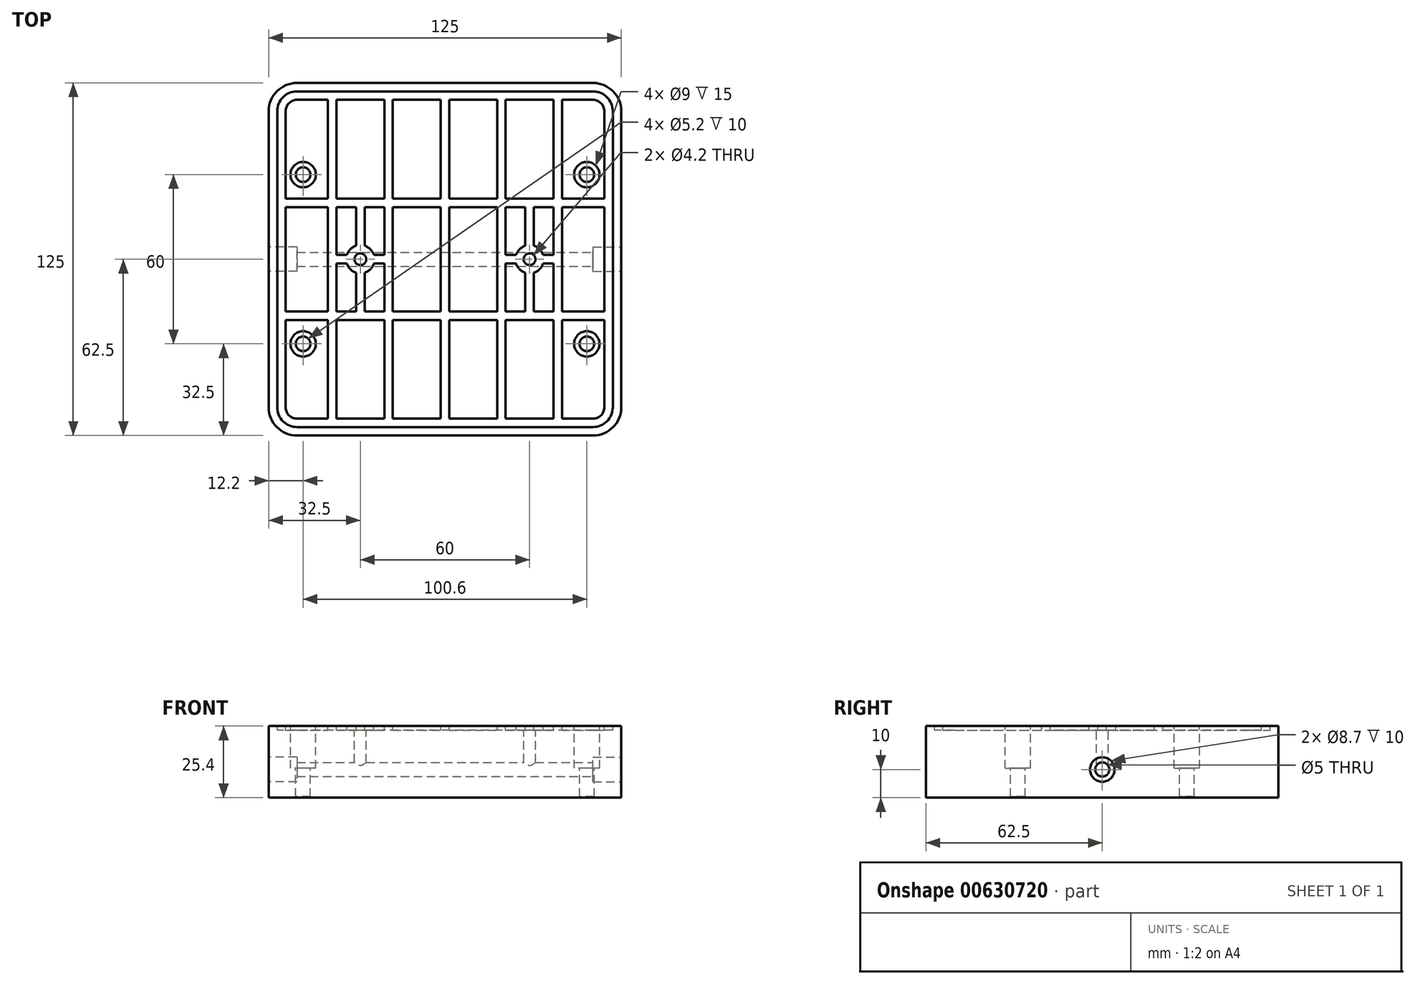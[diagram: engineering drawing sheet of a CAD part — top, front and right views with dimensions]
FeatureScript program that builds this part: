
annotation { "Feature Type Name" : "Feature", "Feature Type Description" : "" }
export const myFeature = defineFeature(function(context is Context, id is Id, definition is map)
    precondition{}
    {
        {
            var Q0;
            Q0=qCreatedBy(makeId("Top.planeOp"),FACE);
            var sketch = newSketch(context, id + "F0", { "sketchPlane" : qUnion([Q0])});
            skLineSegment(sketch, "E0.bottom", {"start": v(57.5, -72.5) * mm, "end": v(-57.5, -72.5) * mm});
            skLineSegment(sketch, "E0.top", {"start": v(57.5, 72.5) * mm, "end": v(-57.5, 72.5) * mm});
            skLineSegment(sketch, "E0.left", {"start": v(62.5, -67.5) * mm, "end": v(62.5, 67.5) * mm});
            skLineSegment(sketch, "E0.right", {"start": v(-62.5, -67.5) * mm, "end": v(-62.5, 67.5) * mm});
            skPoint(sketch, "E0.middle", {"position": v(0, 0) * mm});
            skPoint(sketch, "E1.visualSharp", {"position": v(-62.5, 72.5) * mm});
            skArc(sketch, "E1.filletArc", {"start": v(-57.5, 72.5) * mm, "mid": v(-61.04, 71.04) * mm, "end": v(-62.5, 67.5) * mm});
            skPoint(sketch, "E2.visualSharp", {"position": v(62.5, 72.5) * mm});
            skArc(sketch, "E2.filletArc", {"start": v(62.5, 67.5) * mm, "mid": v(61.04, 71.04) * mm, "end": v(57.5, 72.5) * mm});
            skPoint(sketch, "E3.visualSharp", {"position": v(62.5, -72.5) * mm});
            skArc(sketch, "E3.filletArc", {"start": v(57.5, -72.5) * mm, "mid": v(61.04, -71.04) * mm, "end": v(62.5, -67.5) * mm});
            skPoint(sketch, "E4.visualSharp", {"position": v(-62.5, -72.5) * mm});
            skArc(sketch, "E4.filletArc", {"start": v(-62.5, -67.5) * mm, "mid": v(-61.04, -71.04) * mm, "end": v(-57.5, -72.5) * mm});
            skLineSegment(sketch, "E5", {"start": v(-62.5, 67.5) * mm, "end": v(52.45, 67.5) * mm, "construction": true});
            skLineSegment(sketch, "E6", {"start": v(-48.85, -67.5) * mm, "end": v(50.9, -67.5) * mm, "construction": true});
            skCircle(sketch, "E7", {"center": v(-30, 67.5) * mm, "radius": 2.6 * mm});
            skCircle(sketch, "E8", {"center": v(30, 67.5) * mm, "radius": 2.6 * mm});
            skCircle(sketch, "E9", {"center": v(-30, -67.5) * mm, "radius": 2.6 * mm});
            skCircle(sketch, "E10", {"center": v(30, -67.5) * mm, "radius": 2.6 * mm});
            skSolve(sketch);
        }
        {
            var Q0;
            Q0=makeQuery(id+"F0.imprint","IMPRINT",FACE,{"disambiguationData":[TD([[makeQuery(id+"F0.imprint","IMPRINT",EDGE,{"derivedFrom":sQuery(id+"F0.wireOp",EDGE,"E0.bottom")}),-1.0]])]});
            extrude(context, id + "F1", {"entities" : qUnion([Q0]), "depth" : 9 * mm, "offsetDistance" : 25 * mm});
        }
        {
            var Q0;
            Q0=makeQuery(id+"F1.opExtrude","CAP_FACE",FACE,{"disambiguationData":[OSD([sQuery(id+"F0.wireOp",EDGE,"E0.bottom"),sQuery(id+"F0.wireOp",EDGE,"E0.top"),sQuery(id+"F0.wireOp",EDGE,"E0.left"),sQuery(id+"F0.wireOp",EDGE,"E0.right"),sQuery(id+"F0.wireOp",EDGE,"E1.filletArc"),sQuery(id+"F0.wireOp",EDGE,"E2.filletArc"),sQuery(id+"F0.wireOp",EDGE,"E3.filletArc"),sQuery(id+"F0.wireOp",EDGE,"E4.filletArc"),sQuery(id+"F0.wireOp",EDGE,"E7"),sQuery(id+"F0.wireOp",EDGE,"E8"),sQuery(id+"F0.wireOp",EDGE,"E9"),sQuery(id+"F0.wireOp",EDGE,"E10")])],"isStart":false});
            var sketch = newSketch(context, id + "F2", { "sketchPlane" : qUnion([Q0])});
            skLineSegment(sketch, "E11.bottom", {"start": v(52.5, -62.5) * mm, "end": v(-52.5, -62.5) * mm});
            skLineSegment(sketch, "E11.top", {"start": v(52.5, 62.5) * mm, "end": v(-52.5, 62.5) * mm});
            skLineSegment(sketch, "E11.left", {"start": v(62.5, -52.5) * mm, "end": v(62.5, 52.5) * mm});
            skLineSegment(sketch, "E11.right", {"start": v(-62.5, -52.5) * mm, "end": v(-62.5, 52.5) * mm});
            skPoint(sketch, "E11.middle", {"position": v(0, 0) * mm});
            skPoint(sketch, "E12.visualSharp", {"position": v(-62.5, 62.5) * mm});
            skArc(sketch, "E12.filletArc", {"start": v(-52.5, 62.5) * mm, "mid": v(-59.57, 59.57) * mm, "end": v(-62.5, 52.5) * mm});
            skPoint(sketch, "E13.visualSharp", {"position": v(62.5, 62.5) * mm});
            skArc(sketch, "E13.filletArc", {"start": v(62.5, 52.5) * mm, "mid": v(59.57, 59.57) * mm, "end": v(52.5, 62.5) * mm});
            skPoint(sketch, "E14.visualSharp", {"position": v(62.5, -62.5) * mm});
            skArc(sketch, "E14.filletArc", {"start": v(52.5, -62.5) * mm, "mid": v(59.57, -59.57) * mm, "end": v(62.5, -52.5) * mm});
            skPoint(sketch, "E15.visualSharp", {"position": v(-62.5, -62.5) * mm});
            skArc(sketch, "E15.filletArc", {"start": v(-62.5, -52.5) * mm, "mid": v(-59.57, -59.57) * mm, "end": v(-52.5, -62.5) * mm});
            skSolve(sketch);
        }
        {
            var Q0;
            Q0=makeQuery(id+"F2.imprint","IMPRINT",FACE,{"disambiguationData":[TD([[makeQuery(id+"F2.imprint","IMPRINT",EDGE,{"derivedFrom":sQuery(id+"F2.wireOp",EDGE,"E11.bottom")}),-1.0]])]});
            extrude(context, id + "F3", {"entities" : qUnion([Q0]), "operationType" : NewBodyOperationType.ADD, "depth" : 16.4 * mm, "offsetDistance" : 25 * mm});
        }
        {
            var Q0;
            Q0=makeQuery(id+"F3.boolean.opBoolean","MERGE",FACE,{"derivedFrom":[makeQuery(id+"F1.opExtrude","SWEPT_FACE",FACE,{"disambiguationData":[OSD([sQuery(id+"F0.wireOp",EDGE,"E0.left")])]}),makeQuery(id+"F3.opExtrude","SWEPT_FACE",FACE,{"disambiguationData":[OSD([sQuery(id+"F2.wireOp",EDGE,"E11.left")])]})]});
            var sketch = newSketch(context, id + "F4", { "sketchPlane" : qUnion([Q0])});
            skCircle(sketch, "E16", {"center": v(0, 10) * mm, "radius": 4.35 * mm});
            skCircle(sketch, "E17", {"center": v(0, 10) * mm, "radius": 2.5 * mm});
            skSolve(sketch);
        }
        {
            var Q0;
            Q0=makeQuery(id+"F4.imprint","IMPRINT",FACE,{"disambiguationData":[TD([[makeQuery(id+"F4.imprint","IMPRINT",EDGE,{"derivedFrom":sQuery(id+"F4.wireOp",EDGE,"E17")}),1.0]])]});
            extrude(context, id + "F5", {"entities" : qUnion([Q0]), "operationType" : NewBodyOperationType.REMOVE, "endBound" : BoundingType.THROUGH_ALL, "oppositeDirection" : true, "depth" : 100 * mm, "offsetDistance" : 25 * mm});
        }
        {
            var Q0;
            Q0=makeQuery(id+"F4.imprint","IMPRINT",FACE,{"disambiguationData":[TD([[makeQuery(id+"F4.imprint","IMPRINT",EDGE,{"derivedFrom":sQuery(id+"F4.wireOp",EDGE,"E16")}),1.0]])]});
            extrude(context, id + "F6", {"entities" : qUnion([Q0]), "operationType" : NewBodyOperationType.REMOVE, "oppositeDirection" : true, "depth" : 10 * mm, "offsetDistance" : 25 * mm});
        }
        {
            var Q0;
            {var subQ0=sQuery(id+"F0.wireOp",EDGE,"E4.filletArc");var subQ1=sQuery(id+"F0.wireOp",EDGE,"E10");var subQ2=sQuery(id+"F0.wireOp",EDGE,"E0.left");var subQ3=sQuery(id+"F0.wireOp",EDGE,"E9");var subQ4=sQuery(id+"F0.wireOp",EDGE,"E0.bottom");var subQ5=sQuery(id+"F0.wireOp",EDGE,"E3.filletArc");var subQ6=sQuery(id+"F0.wireOp",EDGE,"E0.right");Q0=makeQuery(id+"F3.boolean.opBoolean","SPLIT",FACE,{"disambiguationData":[TD([makeQuery(id+"F1.opExtrude","SWEPT_FACE",FACE,{"disambiguationData":[OSD([subQ4])]})])],"derivedFrom":makeQuery(id+"F1.opExtrude","CAP_FACE",FACE,{"disambiguationData":[OSD([subQ4,sQuery(id+"F0.wireOp",EDGE,"E0.top"),subQ2,subQ6,sQuery(id+"F0.wireOp",EDGE,"E1.filletArc"),sQuery(id+"F0.wireOp",EDGE,"E2.filletArc"),subQ5,subQ0,sQuery(id+"F0.wireOp",EDGE,"E7"),sQuery(id+"F0.wireOp",EDGE,"E8"),subQ3,subQ1])],"isStart":false})});}
            var Q1;
            {var subQ0=sQuery(id+"F0.wireOp",EDGE,"E8");var subQ1=sQuery(id+"F0.wireOp",EDGE,"E7");var subQ2=sQuery(id+"F0.wireOp",EDGE,"E2.filletArc");var subQ3=sQuery(id+"F0.wireOp",EDGE,"E0.top");var subQ4=sQuery(id+"F0.wireOp",EDGE,"E0.left");var subQ5=sQuery(id+"F0.wireOp",EDGE,"E0.right");var subQ6=sQuery(id+"F0.wireOp",EDGE,"E1.filletArc");Q1=makeQuery(id+"F3.boolean.opBoolean","SPLIT",FACE,{"disambiguationData":[TD([makeQuery(id+"F1.opExtrude","SWEPT_FACE",FACE,{"disambiguationData":[OSD([subQ3])]})])],"derivedFrom":makeQuery(id+"F1.opExtrude","CAP_FACE",FACE,{"disambiguationData":[OSD([sQuery(id+"F0.wireOp",EDGE,"E0.bottom"),subQ3,subQ4,subQ5,subQ6,subQ2,sQuery(id+"F0.wireOp",EDGE,"E3.filletArc"),sQuery(id+"F0.wireOp",EDGE,"E4.filletArc"),subQ1,subQ0,sQuery(id+"F0.wireOp",EDGE,"E9"),sQuery(id+"F0.wireOp",EDGE,"E10")])],"isStart":false})});}
            extrude(context, id + "F7", {"entities" : qUnion([Q0, Q1]), "operationType" : NewBodyOperationType.REMOVE, "oppositeDirection" : true, "depth" : 25 * mm, "offsetDistance" : 25 * mm});
        }
        {
            var Q0;
            Q0=makeQuery(id+"F3.opExtrude","CAP_FACE",FACE,{"disambiguationData":[OSD([sQuery(id+"F2.wireOp",EDGE,"E11.bottom"),sQuery(id+"F2.wireOp",EDGE,"E11.top"),sQuery(id+"F2.wireOp",EDGE,"E11.left"),sQuery(id+"F2.wireOp",EDGE,"E11.right"),sQuery(id+"F2.wireOp",EDGE,"E12.filletArc"),sQuery(id+"F2.wireOp",EDGE,"E13.filletArc"),sQuery(id+"F2.wireOp",EDGE,"E14.filletArc"),sQuery(id+"F2.wireOp",EDGE,"E15.filletArc")])],"isStart":false});
            var sketch = newSketch(context, id + "F8", { "sketchPlane" : qUnion([Q0])});
            skCircle(sketch, "E18", {"center": v(-50.3, 30) * mm, "radius": 4.5 * mm});
            skCircle(sketch, "E19", {"center": v(50.3, 30) * mm, "radius": 4.5 * mm});
            skCircle(sketch, "E20", {"center": v(-50.3, -30) * mm, "radius": 4.5 * mm});
            skCircle(sketch, "E21", {"center": v(50.3, -30) * mm, "radius": 4.5 * mm});
            skLineSegment(sketch, "E22.bottom", {"start": v(24.32, -16.82) * mm, "end": v(-24.32, -16.82) * mm, "construction": true});
            skLineSegment(sketch, "E22.top", {"start": v(24.32, 16.82) * mm, "end": v(-24.32, 16.82) * mm, "construction": true});
            skLineSegment(sketch, "E22.left", {"start": v(24.32, -16.82) * mm, "end": v(24.32, 16.82) * mm, "construction": true});
            skLineSegment(sketch, "E22.right", {"start": v(-24.32, -16.82) * mm, "end": v(-24.32, 16.82) * mm, "construction": true});
            skPoint(sketch, "E22.middle", {"position": v(0, 0) * mm});
            skSolve(sketch);
        }
        {
            var Q0;
            Q0 = qSketchRegion(id + "F8", true);
            extrude(context, id + "F9", {"entities" : qUnion([Q0]), "operationType" : NewBodyOperationType.REMOVE, "oppositeDirection" : true, "depth" : 15 * mm, "offsetDistance" : 25 * mm});
        }
        {
            var Q0;
            Q0=makeQuery(id+"F3.opExtrude","CAP_FACE",FACE,{"disambiguationData":[OSD([sQuery(id+"F2.wireOp",EDGE,"E11.bottom"),sQuery(id+"F2.wireOp",EDGE,"E11.top"),sQuery(id+"F2.wireOp",EDGE,"E11.left"),sQuery(id+"F2.wireOp",EDGE,"E11.right"),sQuery(id+"F2.wireOp",EDGE,"E12.filletArc"),sQuery(id+"F2.wireOp",EDGE,"E13.filletArc"),sQuery(id+"F2.wireOp",EDGE,"E14.filletArc"),sQuery(id+"F2.wireOp",EDGE,"E15.filletArc")])],"isStart":false});
            var sketch = newSketch(context, id + "F10", { "sketchPlane" : qUnion([Q0])});
            skCircle(sketch, "E23", {"center": v(-50.3, 30) * mm, "radius": 4 * mm});
            skCircle(sketch, "E24", {"center": v(50.3, 30) * mm, "radius": 4 * mm});
            skCircle(sketch, "E25", {"center": v(50.3, -30) * mm, "radius": 4 * mm});
            skCircle(sketch, "E26", {"center": v(-50.3, -30) * mm, "radius": 4 * mm});
            skSolve(sketch);
        }
        {
            var Q0;
            Q0=makeQuery(id+"F3.opExtrude","CAP_FACE",FACE,{"disambiguationData":[OSD([sQuery(id+"F2.wireOp",EDGE,"E11.bottom"),sQuery(id+"F2.wireOp",EDGE,"E11.top"),sQuery(id+"F2.wireOp",EDGE,"E11.left"),sQuery(id+"F2.wireOp",EDGE,"E11.right"),sQuery(id+"F2.wireOp",EDGE,"E12.filletArc"),sQuery(id+"F2.wireOp",EDGE,"E13.filletArc"),sQuery(id+"F2.wireOp",EDGE,"E14.filletArc"),sQuery(id+"F2.wireOp",EDGE,"E15.filletArc")])],"isStart":false});
            var sketch = newSketch(context, id + "F11", { "sketchPlane" : qUnion([Q0])});
            skCircle(sketch, "E27", {"center": v(-50.3, 30) * mm, "radius": 2.6 * mm});
            skCircle(sketch, "E28", {"center": v(50.3, 30) * mm, "radius": 2.6 * mm});
            skCircle(sketch, "E29", {"center": v(50.3, -30) * mm, "radius": 2.6 * mm});
            skCircle(sketch, "E30", {"center": v(-50.3, -30) * mm, "radius": 2.6 * mm});
            skSolve(sketch);
        }
        {
            var Q0;
            Q0 = qSketchRegion(id + "F11", true);
            extrude(context, id + "F12", {"entities" : qUnion([Q0]), "operationType" : NewBodyOperationType.REMOVE, "oppositeDirection" : true, "depth" : 25 * mm, "offsetDistance" : 25 * mm});
        }
        {
            var Q0;
            Q0=makeQuery(id+"F3.opExtrude","CAP_FACE",FACE,{"disambiguationData":[OSD([sQuery(id+"F2.wireOp",EDGE,"E11.bottom"),sQuery(id+"F2.wireOp",EDGE,"E11.top"),sQuery(id+"F2.wireOp",EDGE,"E11.left"),sQuery(id+"F2.wireOp",EDGE,"E11.right"),sQuery(id+"F2.wireOp",EDGE,"E12.filletArc"),sQuery(id+"F2.wireOp",EDGE,"E13.filletArc"),sQuery(id+"F2.wireOp",EDGE,"E14.filletArc"),sQuery(id+"F2.wireOp",EDGE,"E15.filletArc")])],"isStart":false});
            var sketch = newSketch(context, id + "F13", { "sketchPlane" : qUnion([Q0])});
            skLineSegment(sketch, "E31.0.0", {"start": v(62.5, -52.5) * mm, "end": v(62.5, 52.5) * mm});
            skArc(sketch, "E31.0.1", {"start": v(62.5, 52.5) * mm, "mid": v(59.57, 59.57) * mm, "end": v(52.5, 62.5) * mm});
            skLineSegment(sketch, "E31.0.2", {"start": v(52.5, 62.5) * mm, "end": v(-52.5, 62.5) * mm});
            skArc(sketch, "E31.0.3", {"start": v(-52.5, 62.5) * mm, "mid": v(-59.57, 59.57) * mm, "end": v(-62.5, 52.5) * mm});
            skLineSegment(sketch, "E31.0.4", {"start": v(-62.5, 52.5) * mm, "end": v(-62.5, -52.5) * mm});
            skArc(sketch, "E31.0.5", {"start": v(-62.5, -52.5) * mm, "mid": v(-59.57, -59.57) * mm, "end": v(-52.5, -62.5) * mm});
            skLineSegment(sketch, "E31.0.6", {"start": v(-52.5, -62.5) * mm, "end": v(52.5, -62.5) * mm});
            skArc(sketch, "E31.0.7", {"start": v(52.5, -62.5) * mm, "mid": v(59.57, -59.57) * mm, "end": v(62.5, -52.5) * mm});
            skArc(sketch, "E32.0", {"start": v(59.5, 52.5) * mm, "mid": v(57.45, 57.45) * mm, "end": v(52.5, 59.5) * mm});
            skLineSegment(sketch, "E32.1", {"start": v(59.5, -52.5) * mm, "end": v(59.5, 52.5) * mm});
            skLineSegment(sketch, "E32.2", {"start": v(52.5, 59.5) * mm, "end": v(-52.5, 59.5) * mm});
            skArc(sketch, "E32.3", {"start": v(52.5, -59.5) * mm, "mid": v(57.45, -57.45) * mm, "end": v(59.5, -52.5) * mm});
            skArc(sketch, "E32.4", {"start": v(-52.5, 59.5) * mm, "mid": v(-57.45, 57.45) * mm, "end": v(-59.5, 52.5) * mm});
            skLineSegment(sketch, "E32.5", {"start": v(-59.5, 52.5) * mm, "end": v(-59.5, -52.5) * mm});
            skArc(sketch, "E32.6", {"start": v(-59.5, -52.5) * mm, "mid": v(-57.45, -57.45) * mm, "end": v(-52.5, -59.5) * mm});
            skLineSegment(sketch, "E32.7", {"start": v(-52.5, -59.5) * mm, "end": v(52.5, -59.5) * mm});
            skLineSegment(sketch, "E33.0", {"start": v(52.5, 56.5) * mm, "end": v(-52.5, 56.5) * mm});
            skArc(sketch, "E33.1", {"start": v(56.5, 52.5) * mm, "mid": v(55.33, 55.33) * mm, "end": v(52.5, 56.5) * mm});
            skArc(sketch, "E33.2", {"start": v(-52.5, 56.5) * mm, "mid": v(-55.33, 55.33) * mm, "end": v(-56.5, 52.5) * mm});
            skLineSegment(sketch, "E33.3", {"start": v(56.5, -52.5) * mm, "end": v(56.5, 52.5) * mm});
            skLineSegment(sketch, "E33.4", {"start": v(-56.5, 52.5) * mm, "end": v(-56.5, -52.5) * mm});
            skArc(sketch, "E33.5", {"start": v(-56.5, -52.5) * mm, "mid": v(-55.33, -55.33) * mm, "end": v(-52.5, -56.5) * mm});
            skLineSegment(sketch, "E33.6", {"start": v(-52.5, -56.5) * mm, "end": v(52.5, -56.5) * mm});
            skArc(sketch, "E33.7", {"start": v(52.5, -56.5) * mm, "mid": v(55.33, -55.33) * mm, "end": v(56.5, -52.5) * mm});
            skLineSegment(sketch, "E34", {"start": v(-56.5, 0) * mm, "end": v(56.5, 0) * mm, "construction": true});
            skLineSegment(sketch, "E35.0.1.0", {"start": v(-56.5, 21.5) * mm, "end": v(56.5, 21.5) * mm});
            skLineSegment(sketch, "E35.0.1.1", {"start": v(-56.5, 18.5) * mm, "end": v(56.5, 18.5) * mm});
            skLineSegment(sketch, "E35.direction1", {"start": v(-56.5, -1.5) * mm, "end": v(-31.5, -1.5) * mm, "construction": true});
            skLineSegment(sketch, "E35.direction2", {"start": v(-56.5, -1.5) * mm, "end": v(-56.5, 18.5) * mm, "construction": true});
            skLineSegment(sketch, "E36.MirrorCS", {"start": v(-56.5, -18.5) * mm, "end": v(56.5, -18.5) * mm});
            skLineSegment(sketch, "E37.MirrorCS", {"start": v(-56.5, -21.5) * mm, "end": v(56.5, -21.5) * mm});
            skSolve(sketch);
        }
        {
            var Q0;
            Q0=makeQuery(id+"F13.imprint","IMPRINT",FACE,{"disambiguationData":[TD([[makeQuery(id+"F13.imprint","IMPRINT",EDGE,{"derivedFrom":sQuery(id+"F13.wireOp",EDGE,"E32.0")}),1.0]])]});
            var Q1;
            {var subQ0=sQuery(id+"F13.wireOp",EDGE,"E35.0.2.0");Q1=makeQuery(id+"F13.imprint","IMPRINT",FACE,{"disambiguationData":[TD([[makeQuery(id+"F13.imprint","IMPRINT",EDGE,{"derivedFrom":subQ0}),-1.0]])]});}
            var Q2;
            {var subQ0=sQuery(id+"F13.wireOp",EDGE,"E35.0.1.0");Q2=makeQuery(id+"F13.imprint","IMPRINT",FACE,{"disambiguationData":[TD([[makeQuery(id+"F13.imprint","IMPRINT",EDGE,{"derivedFrom":subQ0}),-1.0]])]});}
            var Q3;
            {var subQ0=sQuery(id+"F13.wireOp",EDGE,"E36.MirrorCS");Q3=makeQuery(id+"F13.imprint","IMPRINT",FACE,{"disambiguationData":[TD([[makeQuery(id+"F13.imprint","IMPRINT",EDGE,{"derivedFrom":subQ0}),-1.0]])]});}
            var Q4;
            {var subQ0=sQuery(id+"F13.wireOp",EDGE,"df780f31-4266-4d93-95b3-dd8d206b99b12.MirrorCS");Q4=makeQuery(id+"F13.imprint","IMPRINT",FACE,{"disambiguationData":[TD([[makeQuery(id+"F13.imprint","IMPRINT",EDGE,{"derivedFrom":subQ0}),1.0]])]});}
            var Q5;
            {var subQ0=sQuery(id+"F13.wireOp",EDGE,"0d607146-ac1c-4b7b-96e5-c2cd56f04a76.0.left");Q5=makeQuery(id+"F13.imprint","IMPRINT",FACE,{"disambiguationData":[TD([[makeQuery(id+"F13.imprint","IMPRINT",EDGE,{"derivedFrom":subQ0}),-1.0]])]});}
            extrude(context, id + "F14", {"entities" : qUnion([Q0, Q1, Q2, Q3, Q4, Q5]), "operationType" : NewBodyOperationType.REMOVE, "oppositeDirection" : true, "depth" : 1.5 * mm, "offsetDistance" : 25 * mm});
        }
        {
            var Q0;
            Q0=makeQuery(id+"F14.boolean.opBoolean","SPLIT",FACE,{"disambiguationData":[TD([makeQuery(id+"F9.boolean.opBoolean","COPY",FACE,{"derivedFrom":makeQuery(id+"F9.opExtrude","SWEPT_FACE",FACE,{"disambiguationData":[OSD([sQuery(id+"F8.wireOp",EDGE,"E18")])]})})])],"derivedFrom":makeQuery(id+"F3.opExtrude","CAP_FACE",FACE,{"disambiguationData":[OSD([sQuery(id+"F2.wireOp",EDGE,"E11.bottom"),sQuery(id+"F2.wireOp",EDGE,"E11.top"),sQuery(id+"F2.wireOp",EDGE,"E11.left"),sQuery(id+"F2.wireOp",EDGE,"E11.right"),sQuery(id+"F2.wireOp",EDGE,"E12.filletArc"),sQuery(id+"F2.wireOp",EDGE,"E13.filletArc"),sQuery(id+"F2.wireOp",EDGE,"E14.filletArc"),sQuery(id+"F2.wireOp",EDGE,"E15.filletArc")])],"isStart":false})});
            var sketch = newSketch(context, id + "F15", { "sketchPlane" : qUnion([Q0])});
            skLineSegment(sketch, "E38", {"start": v(0, -56.5) * mm, "end": v(0, 56.5) * mm, "construction": true});
            skLineSegment(sketch, "E39.0.left", {"start": v(-1.5, -56.5) * mm, "end": v(-1.5, 56.5) * mm});
            skLineSegment(sketch, "E39.0.right", {"start": v(1.5, -56.5) * mm, "end": v(1.5, 56.5) * mm});
            skLineSegment(sketch, "E40.1.0.0", {"start": v(18.5, -56.5) * mm, "end": v(18.5, 56.5) * mm});
            skLineSegment(sketch, "E40.1.0.1", {"start": v(21.5, -56.5) * mm, "end": v(21.5, 56.5) * mm});
            skLineSegment(sketch, "E40.2.0.0", {"start": v(38.5, -56.5) * mm, "end": v(38.5, 56.5) * mm});
            skLineSegment(sketch, "E40.2.0.1", {"start": v(41.5, -56.5) * mm, "end": v(41.5, 56.5) * mm});
            skLineSegment(sketch, "E40.direction1", {"start": v(-1.5, -56.5) * mm, "end": v(18.5, -56.5) * mm, "construction": true});
            skLineSegment(sketch, "E41.MirrorCS", {"start": v(-41.5, -56.5) * mm, "end": v(-41.5, 56.5) * mm});
            skLineSegment(sketch, "E42.MirrorCS", {"start": v(-38.5, -56.5) * mm, "end": v(-38.5, 56.5) * mm});
            skLineSegment(sketch, "E43.MirrorCS", {"start": v(-18.5, -56.5) * mm, "end": v(-18.5, 56.5) * mm});
            skLineSegment(sketch, "E44.MirrorCS", {"start": v(-21.5, -56.5) * mm, "end": v(-21.5, 56.5) * mm});
            skLineSegment(sketch, "E45", {"start": v(-41.5, 56.5) * mm, "end": v(41.5, 56.5) * mm});
            skLineSegment(sketch, "E46", {"start": v(41.5, -56.5) * mm, "end": v(-41.5, -56.5) * mm});
            skSolve(sketch);
        }
        {
            var Q0;
            {var subQ0=sQuery(id+"F15.wireOp",EDGE,"E45");var subQ1=sQuery(id+"F15.wireOp",EDGE,"E41.MirrorCS");var subQ2=makeQuery(id+"F15.imprint","INTERSECT",VERTEX,{"derivedFrom":[subQ1,subQ0]});Q0=makeQuery(id+"F15.imprint","IMPRINT",FACE,{"disambiguationData":[TD([[makeQuery(id+"F15.imprint","IMPRINT",EDGE,{"disambiguationData":[TD([[subQ2,1.0]])],"derivedFrom":subQ1}),-1.0]])]});}
            var Q1;
            {var subQ0=sQuery(id+"F15.wireOp",EDGE,"E41.MirrorCS");var subQ1=makeQuery(id+"F14.boolean.opBoolean","COPY",EDGE,{"derivedFrom":makeQuery(id+"F14.opExtrude","CAP_EDGE",EDGE,{"disambiguationData":[OSD([sQuery(id+"F13.wireOp",EDGE,"E35.0.1.0")])],"isStart":true})});var subQ2=makeQuery(id+"F15.imprint","INTERSECT",VERTEX,{"derivedFrom":[subQ1,subQ0]});Q1=makeQuery(id+"F15.imprint","IMPRINT",FACE,{"disambiguationData":[TD([[makeQuery(id+"F15.imprint","IMPRINT",EDGE,{"disambiguationData":[TD([[subQ2,-1.0]])],"derivedFrom":subQ0}),-1.0]])]});}
            var Q2;
            {var subQ0=sQuery(id+"F15.wireOp",EDGE,"E46");var subQ1=sQuery(id+"F15.wireOp",EDGE,"E41.MirrorCS");var subQ2=makeQuery(id+"F15.imprint","INTERSECT",VERTEX,{"derivedFrom":[subQ1,subQ0]});Q2=makeQuery(id+"F15.imprint","IMPRINT",FACE,{"disambiguationData":[TD([[makeQuery(id+"F15.imprint","IMPRINT",EDGE,{"disambiguationData":[TD([[subQ2,-1.0]])],"derivedFrom":subQ1}),-1.0]])]});}
            var Q3;
            {var subQ0=sQuery(id+"F15.wireOp",EDGE,"E45");var subQ1=sQuery(id+"F15.wireOp",EDGE,"E43.MirrorCS");var subQ2=makeQuery(id+"F15.imprint","INTERSECT",VERTEX,{"derivedFrom":[subQ1,subQ0]});Q3=makeQuery(id+"F15.imprint","IMPRINT",FACE,{"disambiguationData":[TD([[makeQuery(id+"F15.imprint","IMPRINT",EDGE,{"disambiguationData":[TD([[subQ2,1.0]])],"derivedFrom":subQ1}),1.0]])]});}
            var Q4;
            {var subQ0=sQuery(id+"F15.wireOp",EDGE,"E43.MirrorCS");var subQ1=makeQuery(id+"F14.boolean.opBoolean","COPY",EDGE,{"derivedFrom":makeQuery(id+"F14.opExtrude","CAP_EDGE",EDGE,{"disambiguationData":[OSD([sQuery(id+"F13.wireOp",EDGE,"E35.0.1.0")])],"isStart":true})});var subQ2=makeQuery(id+"F15.imprint","INTERSECT",VERTEX,{"derivedFrom":[subQ1,subQ0]});Q4=makeQuery(id+"F15.imprint","IMPRINT",FACE,{"disambiguationData":[TD([[makeQuery(id+"F15.imprint","IMPRINT",EDGE,{"disambiguationData":[TD([[subQ2,-1.0]])],"derivedFrom":subQ0}),1.0]])]});}
            var Q5;
            {var subQ0=sQuery(id+"F15.wireOp",EDGE,"E46");var subQ1=sQuery(id+"F15.wireOp",EDGE,"E43.MirrorCS");var subQ2=makeQuery(id+"F15.imprint","INTERSECT",VERTEX,{"derivedFrom":[subQ1,subQ0]});Q5=makeQuery(id+"F15.imprint","IMPRINT",FACE,{"disambiguationData":[TD([[makeQuery(id+"F15.imprint","IMPRINT",EDGE,{"disambiguationData":[TD([[subQ2,-1.0]])],"derivedFrom":subQ1}),1.0]])]});}
            var Q6;
            {var subQ0=sQuery(id+"F15.wireOp",EDGE,"E45");var subQ1=sQuery(id+"F15.wireOp",EDGE,"E39.0.left");var subQ2=makeQuery(id+"F15.imprint","INTERSECT",VERTEX,{"derivedFrom":[subQ1,subQ0]});Q6=makeQuery(id+"F15.imprint","IMPRINT",FACE,{"disambiguationData":[TD([[makeQuery(id+"F15.imprint","IMPRINT",EDGE,{"disambiguationData":[TD([[subQ2,1.0]])],"derivedFrom":subQ1}),-1.0]])]});}
            var Q7;
            {var subQ0=sQuery(id+"F15.wireOp",EDGE,"E39.0.left");var subQ1=makeQuery(id+"F14.boolean.opBoolean","COPY",EDGE,{"derivedFrom":makeQuery(id+"F14.opExtrude","CAP_EDGE",EDGE,{"disambiguationData":[OSD([sQuery(id+"F13.wireOp",EDGE,"E35.0.1.0")])],"isStart":true})});var subQ2=makeQuery(id+"F15.imprint","INTERSECT",VERTEX,{"derivedFrom":[subQ1,subQ0]});Q7=makeQuery(id+"F15.imprint","IMPRINT",FACE,{"disambiguationData":[TD([[makeQuery(id+"F15.imprint","IMPRINT",EDGE,{"disambiguationData":[TD([[subQ2,-1.0]])],"derivedFrom":subQ0}),-1.0]])]});}
            var Q8;
            {var subQ0=sQuery(id+"F15.wireOp",EDGE,"E46");var subQ1=sQuery(id+"F15.wireOp",EDGE,"E39.0.left");var subQ2=makeQuery(id+"F15.imprint","INTERSECT",VERTEX,{"derivedFrom":[subQ1,subQ0]});Q8=makeQuery(id+"F15.imprint","IMPRINT",FACE,{"disambiguationData":[TD([[makeQuery(id+"F15.imprint","IMPRINT",EDGE,{"disambiguationData":[TD([[subQ2,-1.0]])],"derivedFrom":subQ1}),-1.0]])]});}
            var Q9;
            {var subQ0=sQuery(id+"F15.wireOp",EDGE,"E46");var subQ1=sQuery(id+"F15.wireOp",EDGE,"E40.1.0.0");var subQ2=makeQuery(id+"F15.imprint","INTERSECT",VERTEX,{"derivedFrom":[subQ1,subQ0]});Q9=makeQuery(id+"F15.imprint","IMPRINT",FACE,{"disambiguationData":[TD([[makeQuery(id+"F15.imprint","IMPRINT",EDGE,{"disambiguationData":[TD([[subQ2,-1.0]])],"derivedFrom":subQ1}),-1.0]])]});}
            var Q10;
            {var subQ0=sQuery(id+"F15.wireOp",EDGE,"E40.1.0.0");var subQ1=makeQuery(id+"F14.boolean.opBoolean","COPY",EDGE,{"derivedFrom":makeQuery(id+"F14.opExtrude","CAP_EDGE",EDGE,{"disambiguationData":[OSD([sQuery(id+"F13.wireOp",EDGE,"E35.0.1.0")])],"isStart":true})});var subQ2=makeQuery(id+"F15.imprint","INTERSECT",VERTEX,{"derivedFrom":[subQ1,subQ0]});Q10=makeQuery(id+"F15.imprint","IMPRINT",FACE,{"disambiguationData":[TD([[makeQuery(id+"F15.imprint","IMPRINT",EDGE,{"disambiguationData":[TD([[subQ2,-1.0]])],"derivedFrom":subQ0}),-1.0]])]});}
            var Q11;
            {var subQ0=sQuery(id+"F15.wireOp",EDGE,"E45");var subQ1=sQuery(id+"F15.wireOp",EDGE,"E40.1.0.0");var subQ2=makeQuery(id+"F15.imprint","INTERSECT",VERTEX,{"derivedFrom":[subQ1,subQ0]});Q11=makeQuery(id+"F15.imprint","IMPRINT",FACE,{"disambiguationData":[TD([[makeQuery(id+"F15.imprint","IMPRINT",EDGE,{"disambiguationData":[TD([[subQ2,1.0]])],"derivedFrom":subQ1}),-1.0]])]});}
            var Q12;
            {var subQ0=sQuery(id+"F15.wireOp",EDGE,"E45");var subQ1=sQuery(id+"F15.wireOp",EDGE,"E40.2.0.0");var subQ2=makeQuery(id+"F15.imprint","INTERSECT",VERTEX,{"derivedFrom":[subQ1,subQ0]});Q12=makeQuery(id+"F15.imprint","IMPRINT",FACE,{"disambiguationData":[TD([[makeQuery(id+"F15.imprint","IMPRINT",EDGE,{"disambiguationData":[TD([[subQ2,1.0]])],"derivedFrom":subQ1}),-1.0]])]});}
            var Q13;
            {var subQ0=sQuery(id+"F15.wireOp",EDGE,"E40.2.0.0");var subQ1=makeQuery(id+"F14.boolean.opBoolean","COPY",EDGE,{"derivedFrom":makeQuery(id+"F14.opExtrude","CAP_EDGE",EDGE,{"disambiguationData":[OSD([sQuery(id+"F13.wireOp",EDGE,"E35.0.1.0")])],"isStart":true})});var subQ2=makeQuery(id+"F15.imprint","INTERSECT",VERTEX,{"derivedFrom":[subQ1,subQ0]});Q13=makeQuery(id+"F15.imprint","IMPRINT",FACE,{"disambiguationData":[TD([[makeQuery(id+"F15.imprint","IMPRINT",EDGE,{"disambiguationData":[TD([[subQ2,-1.0]])],"derivedFrom":subQ0}),-1.0]])]});}
            var Q14;
            {var subQ0=sQuery(id+"F15.wireOp",EDGE,"E46");var subQ1=sQuery(id+"F15.wireOp",EDGE,"E40.2.0.0");var subQ2=makeQuery(id+"F15.imprint","INTERSECT",VERTEX,{"derivedFrom":[subQ1,subQ0]});Q14=makeQuery(id+"F15.imprint","IMPRINT",FACE,{"disambiguationData":[TD([[makeQuery(id+"F15.imprint","IMPRINT",EDGE,{"disambiguationData":[TD([[subQ2,-1.0]])],"derivedFrom":subQ1}),-1.0]])]});}
            extrude(context, id + "F16", {"entities" : qUnion([Q0, Q1, Q2, Q3, Q4, Q5, Q6, Q7, Q8, Q9, Q10, Q11, Q12, Q13, Q14]), "operationType" : NewBodyOperationType.REMOVE, "oppositeDirection" : true, "depth" : 1.5 * mm, "offsetDistance" : 25 * mm});
        }
        {
            var Q0;
            {var subQ0=sQuery(id+"F13.wireOp",EDGE,"E35.0.1.1");var subQ1=makeQuery(id+"F14.opExtrude","SWEPT_FACE",FACE,{"disambiguationData":[OSD([subQ0])]});Q0=makeQuery(id+"F16.boolean.opBoolean","SPLIT",FACE,{"disambiguationData":[TD([makeQuery(id+"F16.opExtrude","SWEPT_FACE",FACE,{"disambiguationData":[OSD([sQuery(id+"F15.wireOp",EDGE,"E42.MirrorCS")])]})])],"derivedFrom":makeQuery(id+"F14.boolean.opBoolean","SPLIT",FACE,{"disambiguationData":[TD([subQ1])],"derivedFrom":makeQuery(id+"F3.opExtrude","CAP_FACE",FACE,{"disambiguationData":[OSD([sQuery(id+"F2.wireOp",EDGE,"E11.bottom"),sQuery(id+"F2.wireOp",EDGE,"E11.top"),sQuery(id+"F2.wireOp",EDGE,"E11.left"),sQuery(id+"F2.wireOp",EDGE,"E11.right"),sQuery(id+"F2.wireOp",EDGE,"E12.filletArc"),sQuery(id+"F2.wireOp",EDGE,"E13.filletArc"),sQuery(id+"F2.wireOp",EDGE,"E14.filletArc"),sQuery(id+"F2.wireOp",EDGE,"E15.filletArc")])],"isStart":false})})});}
            var sketch = newSketch(context, id + "F17", { "sketchPlane" : qUnion([Q0])});
            skCircle(sketch, "E47", {"center": v(-30, 0) * mm, "radius": 2.1 * mm});
            skCircle(sketch, "E48", {"center": v(30, 0) * mm, "radius": 2.1 * mm});
            skSolve(sketch);
        }
        {
            var Q0;
            Q0 = qSketchRegion(id + "F17", true);
            extrude(context, id + "F18", {"entities" : qUnion([Q0]), "operationType" : NewBodyOperationType.REMOVE, "oppositeDirection" : true, "depth" : 16 * mm, "offsetDistance" : 25 * mm});
        }
        {
            var Q0;
            {var subQ0=sQuery(id+"F13.wireOp",EDGE,"E35.0.1.1");var subQ1=makeQuery(id+"F14.opExtrude","SWEPT_FACE",FACE,{"disambiguationData":[OSD([subQ0])]});Q0=makeQuery(id+"F16.boolean.opBoolean","SPLIT",FACE,{"disambiguationData":[TD([makeQuery(id+"F16.opExtrude","SWEPT_FACE",FACE,{"disambiguationData":[OSD([sQuery(id+"F15.wireOp",EDGE,"E42.MirrorCS")])]})])],"derivedFrom":makeQuery(id+"F14.boolean.opBoolean","SPLIT",FACE,{"disambiguationData":[TD([subQ1])],"derivedFrom":makeQuery(id+"F3.opExtrude","CAP_FACE",FACE,{"disambiguationData":[OSD([sQuery(id+"F2.wireOp",EDGE,"E11.bottom"),sQuery(id+"F2.wireOp",EDGE,"E11.top"),sQuery(id+"F2.wireOp",EDGE,"E11.left"),sQuery(id+"F2.wireOp",EDGE,"E11.right"),sQuery(id+"F2.wireOp",EDGE,"E12.filletArc"),sQuery(id+"F2.wireOp",EDGE,"E13.filletArc"),sQuery(id+"F2.wireOp",EDGE,"E14.filletArc"),sQuery(id+"F2.wireOp",EDGE,"E15.filletArc")])],"isStart":false})})});}
            var sketch = newSketch(context, id + "F19", { "sketchPlane" : qUnion([Q0])});
            skCircle(sketch, "E49", {"center": v(-30, 0) * mm, "radius": 5 * mm});
            skCircle(sketch, "E50", {"center": v(30, 0) * mm, "radius": 5 * mm});
            skSolve(sketch);
        }
        {
            var Q0;
            Q0 = qSketchRegion(id + "F19", true);
            extrude(context, id + "F20", {"entities" : qUnion([Q0]), "operationType" : NewBodyOperationType.REMOVE, "oppositeDirection" : true, "depth" : 1.5 * mm, "offsetDistance" : 25 * mm});
        }
        {
            var Q0;
            {var subQ0=sQuery(id+"F13.wireOp",EDGE,"E35.0.1.1");var subQ1=makeQuery(id+"F14.opExtrude","SWEPT_FACE",FACE,{"disambiguationData":[OSD([subQ0])]});Q0=makeQuery(id+"F16.boolean.opBoolean","SPLIT",FACE,{"disambiguationData":[TD([makeQuery(id+"F16.opExtrude","SWEPT_FACE",FACE,{"disambiguationData":[OSD([sQuery(id+"F15.wireOp",EDGE,"E42.MirrorCS")])]})])],"derivedFrom":makeQuery(id+"F14.boolean.opBoolean","SPLIT",FACE,{"disambiguationData":[TD([subQ1])],"derivedFrom":makeQuery(id+"F3.opExtrude","CAP_FACE",FACE,{"disambiguationData":[OSD([sQuery(id+"F2.wireOp",EDGE,"E11.bottom"),sQuery(id+"F2.wireOp",EDGE,"E11.top"),sQuery(id+"F2.wireOp",EDGE,"E11.left"),sQuery(id+"F2.wireOp",EDGE,"E11.right"),sQuery(id+"F2.wireOp",EDGE,"E12.filletArc"),sQuery(id+"F2.wireOp",EDGE,"E13.filletArc"),sQuery(id+"F2.wireOp",EDGE,"E14.filletArc"),sQuery(id+"F2.wireOp",EDGE,"E15.filletArc")])],"isStart":false})})});}
            var sketch = newSketch(context, id + "F21", { "sketchPlane" : qUnion([Q0])});
            skLineSegment(sketch, "E51", {"start": v(-38.5, 0) * mm, "end": v(-21.5, 0) * mm, "construction": true});
            skLineSegment(sketch, "E52", {"start": v(21.5, 0) * mm, "end": v(38.5, 0) * mm, "construction": true});
            skLineSegment(sketch, "E53", {"start": v(-30, 18.5) * mm, "end": v(-30, -18.5) * mm, "construction": true});
            skLineSegment(sketch, "E54", {"start": v(30, 18.5) * mm, "end": v(30, -18.5) * mm, "construction": true});
            skArc(sketch, "E55.0.startCap", {"start": v(28.5, 18.5) * mm, "mid": v(30, 20) * mm, "end": v(31.5, 18.5) * mm});
            skArc(sketch, "E55.0.endCap", {"start": v(31.5, -18.5) * mm, "mid": v(30, -20) * mm, "end": v(28.5, -18.5) * mm});
            skLineSegment(sketch, "E55.0.left", {"start": v(31.5, 18.5) * mm, "end": v(31.5, -18.5) * mm});
            skLineSegment(sketch, "E55.0.right", {"start": v(28.5, 18.5) * mm, "end": v(28.5, -18.5) * mm});
            skArc(sketch, "E55.1.startCap", {"start": v(21.5, -1.5) * mm, "mid": v(20, 0) * mm, "end": v(21.5, 1.5) * mm});
            skArc(sketch, "E55.1.endCap", {"start": v(38.5, 1.5) * mm, "mid": v(40, 0) * mm, "end": v(38.5, -1.5) * mm});
            skLineSegment(sketch, "E55.1.left", {"start": v(21.5, 1.5) * mm, "end": v(38.5, 1.5) * mm});
            skLineSegment(sketch, "E55.1.right", {"start": v(21.5, -1.5) * mm, "end": v(38.5, -1.5) * mm});
            skArc(sketch, "E55.2.startCap", {"start": v(-38.5, -1.5) * mm, "mid": v(-40, 0) * mm, "end": v(-38.5, 1.5) * mm});
            skArc(sketch, "E55.2.endCap", {"start": v(-21.5, 1.5) * mm, "mid": v(-20, 0) * mm, "end": v(-21.5, -1.5) * mm});
            skLineSegment(sketch, "E55.2.left", {"start": v(-38.5, 1.5) * mm, "end": v(-21.5, 1.5) * mm});
            skLineSegment(sketch, "E55.2.right", {"start": v(-38.5, -1.5) * mm, "end": v(-21.5, -1.5) * mm});
            skArc(sketch, "E55.3.startCap", {"start": v(-31.5, 18.5) * mm, "mid": v(-30, 20) * mm, "end": v(-28.5, 18.5) * mm});
            skArc(sketch, "E55.3.endCap", {"start": v(-28.5, -18.5) * mm, "mid": v(-30, -20) * mm, "end": v(-31.5, -18.5) * mm});
            skLineSegment(sketch, "E55.3.left", {"start": v(-28.5, 18.5) * mm, "end": v(-28.5, -18.5) * mm});
            skLineSegment(sketch, "E55.3.right", {"start": v(-31.5, 18.5) * mm, "end": v(-31.5, -18.5) * mm});
            skSolve(sketch);
        }
        {
            var Q0;
            Q0 = qSketchRegion(id + "F21", true);
            extrude(context, id + "F22", {"entities" : qUnion([Q0]), "operationType" : NewBodyOperationType.REMOVE, "oppositeDirection" : true, "depth" : 1.5 * mm, "offsetDistance" : 25 * mm});
        }
        {
            var Q0;
            Q0=makeQuery(id+"F3.boolean.opBoolean","MERGE",FACE,{"derivedFrom":[makeQuery(id+"F1.opExtrude","SWEPT_FACE",FACE,{"disambiguationData":[OSD([sQuery(id+"F0.wireOp",EDGE,"E0.right")])]}),makeQuery(id+"F3.opExtrude","SWEPT_FACE",FACE,{"disambiguationData":[OSD([sQuery(id+"F2.wireOp",EDGE,"E11.right")])]})]});
            var sketch = newSketch(context, id + "F23", { "sketchPlane" : qUnion([Q0])});
            skCircle(sketch, "E56", {"center": v(0, 10) * mm, "radius": 4.35 * mm});
            skSolve(sketch);
        }
        {
            var Q0;
            Q0=makeQuery(id+"F23.imprint","IMPRINT",FACE,{"disambiguationData":[TD([[makeQuery(id+"F23.imprint","IMPRINT",EDGE,{"derivedFrom":sQuery(id+"F23.wireOp",EDGE,"E56")}),1.0]])]});
            extrude(context, id + "F24", {"entities" : qUnion([Q0]), "operationType" : NewBodyOperationType.REMOVE, "oppositeDirection" : true, "depth" : 10 * mm, "offsetDistance" : 25 * mm});
        }
    });
